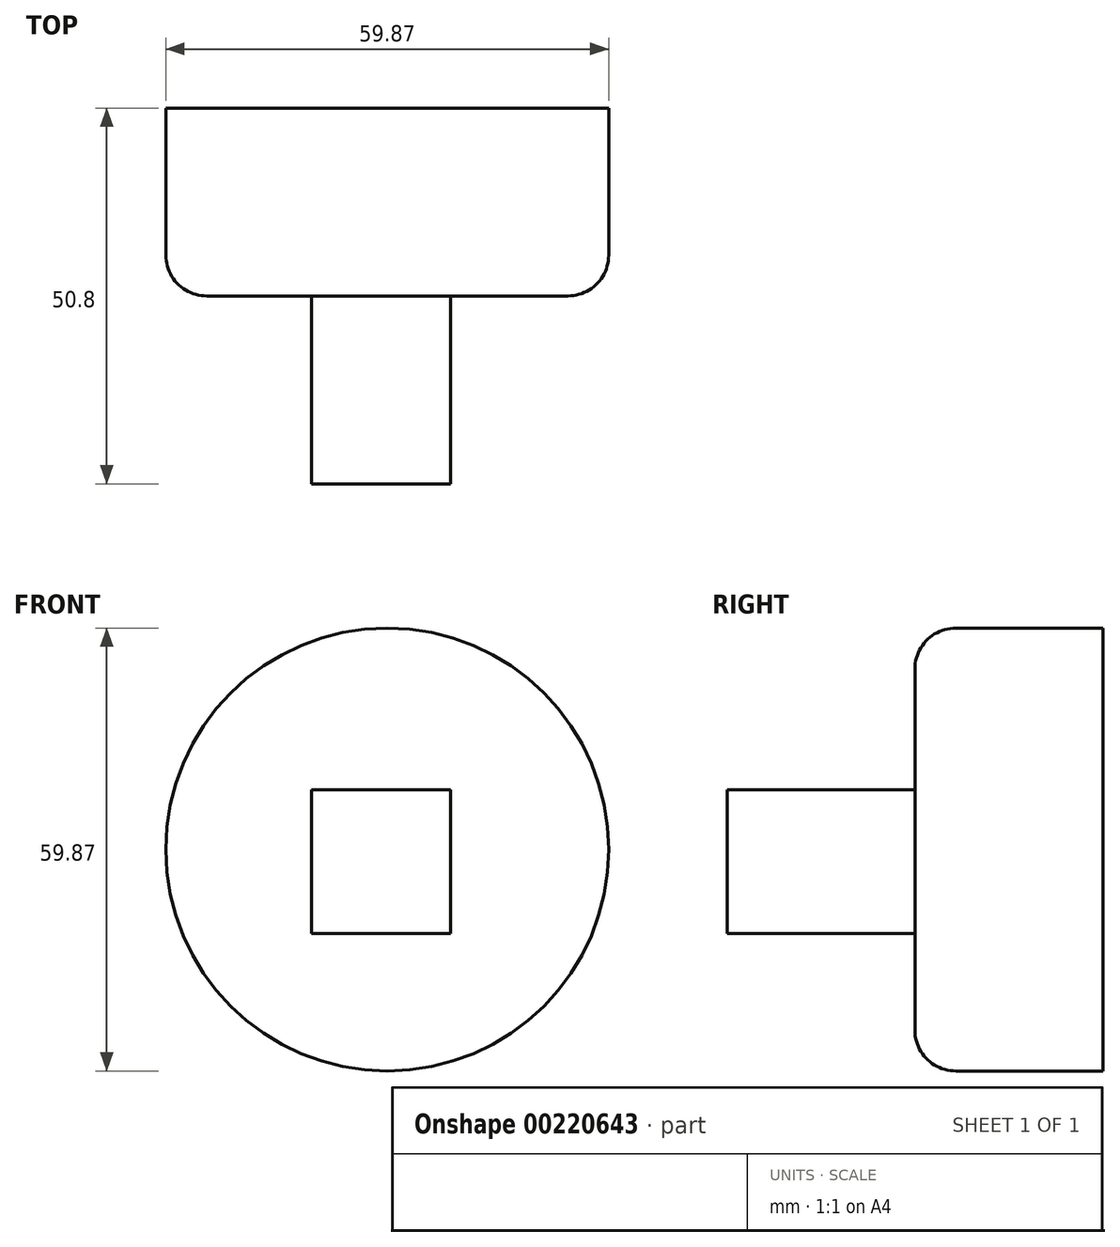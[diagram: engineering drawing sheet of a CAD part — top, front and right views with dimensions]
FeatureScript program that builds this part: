
annotation { "Feature Type Name" : "Feature", "Feature Type Description" : "" }
export const myFeature = defineFeature(function(context is Context, id is Id, definition is map)
    precondition{}
    {
        {
            var Q0;
            Q0=qCreatedBy(makeId("Front.planeOp"),FACE);
            var sketch = newSketch(context, id + "F0", { "sketchPlane" : qUnion([Q0])});
            skCircle(sketch, "E0", {"center": v(-61.49, 39.14) * mm, "radius": 29.94 * mm});
            skSolve(sketch);
        }
        {
            var Q0;
            Q0 = qSketchRegion(id + "F0", true);
            extrude(context, id + "F1", {"entities" : qUnion([Q0]), "depth" : 25.4 * mm});
        }
        {
            var Q0;
            Q0=makeQuery(id+"F1.opExtrude","CAP_EDGE",EDGE,{"disambiguationData":[OSD([sQuery(id+"F0.wireOp",EDGE,"E0")])],"isStart":false});
            fillet(context, id + "F2", {"entities" : qUnion([Q0]), "radius" : 5.52 * mm, "tangentPropagation" : true, "allowEdgeOverflow" : false});
        }
        {
            var Q0;
            Q0=makeQuery(id+"F1.opExtrude","CAP_FACE",FACE,{"disambiguationData":[OSD([sQuery(id+"F0.wireOp",EDGE,"E0")])],"isStart":false});
            var sketch = newSketch(context, id + "F3", { "sketchPlane" : qUnion([Q0])});
            skLineSegment(sketch, "E1.bottom", {"start": v(-71.7, 47.2) * mm, "end": v(-52.95, 47.2) * mm});
            skLineSegment(sketch, "E1.top", {"start": v(-71.7, 27.8) * mm, "end": v(-52.95, 27.8) * mm});
            skLineSegment(sketch, "E1.left", {"start": v(-71.7, 47.2) * mm, "end": v(-71.7, 27.8) * mm});
            skLineSegment(sketch, "E1.right", {"start": v(-52.95, 47.2) * mm, "end": v(-52.95, 27.8) * mm});
            skSolve(sketch);
        }
        {
            var Q0;
            Q0 = qSketchRegion(id + "F3", true);
            extrude(context, id + "F4", {"entities" : qUnion([Q0]), "operationType" : NewBodyOperationType.ADD, "depth" : 25.4 * mm});
        }
    });
